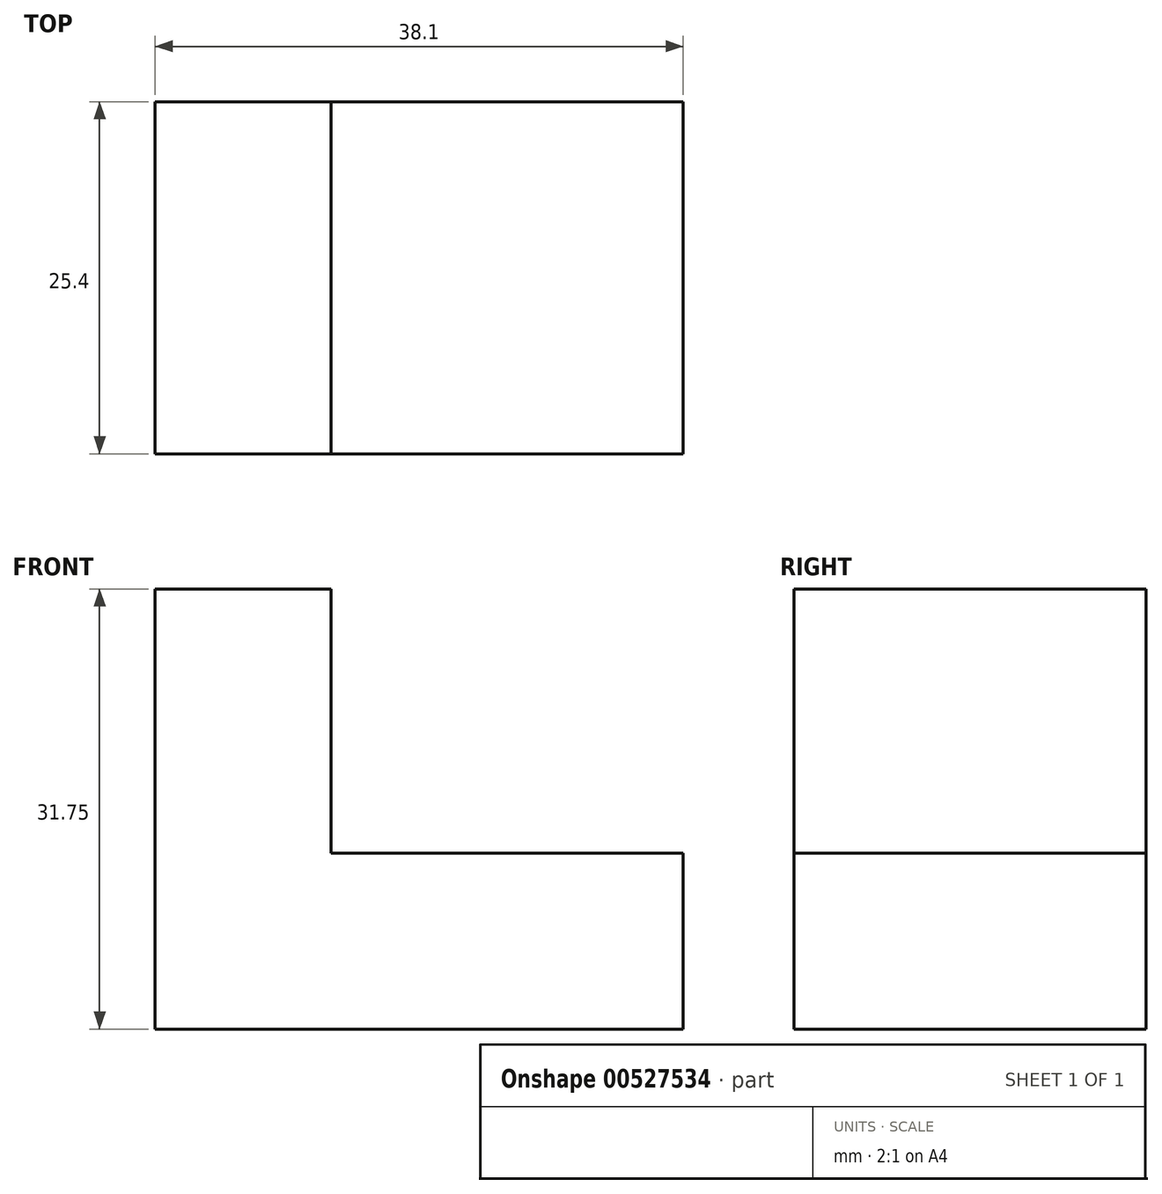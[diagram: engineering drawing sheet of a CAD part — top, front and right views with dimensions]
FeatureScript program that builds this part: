
annotation { "Feature Type Name" : "Feature", "Feature Type Description" : "" }
export const myFeature = defineFeature(function(context is Context, id is Id, definition is map)
    precondition{}
    {
        {
            var Q0;
            Q0=qCreatedBy(makeId("Front.planeOp"),FACE);
            var sketch = newSketch(context, id + "F0", { "sketchPlane" : qUnion([Q0])});
            skLineSegment(sketch, "E0", {"start": v(0, 0) * mm, "end": v(38.1, 0) * mm});
            skLineSegment(sketch, "E1", {"start": v(38.1, 0) * mm, "end": v(38.1, 12.7) * mm});
            skLineSegment(sketch, "E2", {"start": v(38.1, 12.7) * mm, "end": v(12.7, 12.7) * mm});
            skLineSegment(sketch, "E3", {"start": v(12.7, 12.7) * mm, "end": v(12.7, 31.75) * mm});
            skLineSegment(sketch, "E4", {"start": v(12.7, 31.75) * mm, "end": v(0, 31.75) * mm});
            skLineSegment(sketch, "E5", {"start": v(0, 31.75) * mm, "end": v(0, 0) * mm});
            skSolve(sketch);
        }
        {
            var Q0;
            Q0=makeQuery(id+"F0.imprint","IMPRINT",FACE,{"disambiguationData":[TD([[makeQuery(id+"F0.imprint","IMPRINT",EDGE,{"derivedFrom":sQuery(id+"F0.wireOp",EDGE,"E0")}),1.0]])]});
            extrude(context, id + "F1", {"entities" : qUnion([Q0]), "oppositeDirection" : true, "depth" : 25.4 * mm, "offsetDistance" : 25.4 * mm});
        }
    });
